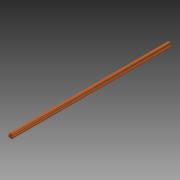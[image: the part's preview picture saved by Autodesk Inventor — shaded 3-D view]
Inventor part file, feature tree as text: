
AUTODESK INVENTOR PART (.ipt)
format: ipt  version: 2015 (Build 190159000, 159)  size: 88,064 bytes
history: native  units: in
note: dims shown in document units (in); Inventor stores cm internally (conversion verified against a paired STEP export)
features: extrude x1, sketch x1
ambient origin geometry x8: Origin, YZ Plane, XZ Plane, XY Plane, X Axis, Y Axis, Z Axis, Center Point
bodies: Solid1 (feature_tree)
feature tree (2):
  extrude  "Extrusion1"  Depth=0.6in
  sketch  "Sketch1"  dims[d0=1.0in d2=0.6in d3=0.5in d9=0.1in d10=0.1in d11=1.0in d13=0.25in d14=0.5in d15=0.5in d16=0.5in d17=0.25in d18=70.0in d19=0.0in]
